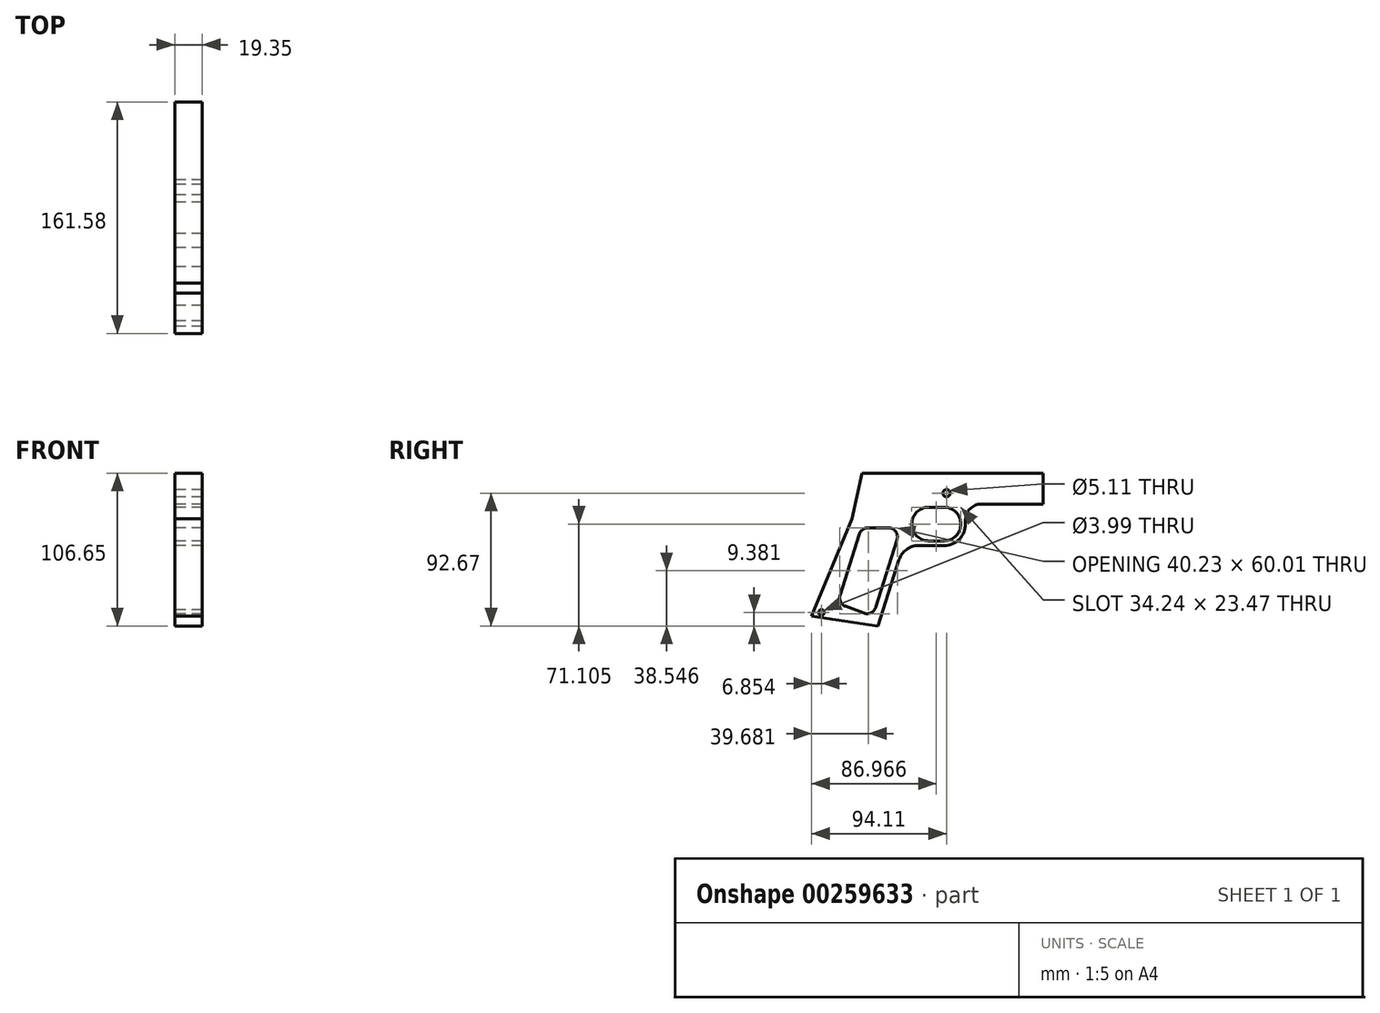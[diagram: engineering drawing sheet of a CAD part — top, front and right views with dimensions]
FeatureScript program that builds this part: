
annotation { "Feature Type Name" : "Feature", "Feature Type Description" : "" }
export const myFeature = defineFeature(function(context is Context, id is Id, definition is map)
    precondition{}
    {
        {
            var Q0;
            Q0=qCreatedBy(makeId("Right.planeOp"),FACE);
            var sketch = newSketch(context, id + "F0", { "sketchPlane" : qUnion([Q0])});
            skCircle(sketch, "E0", {"center": v(0, 0) * mm, "radius": 2.55 * mm});
            skLineSegment(sketch, "E1", {"start": v(-54.8, -24.12) * mm, "end": v(-40.65, -24.12) * mm});
            skLineSegment(sketch, "E2", {"start": v(-60.85, -28.56) * mm, "end": v(-74.27, -71.12) * mm});
            skLineSegment(sketch, "E3", {"start": v(-49.51, -79.7) * mm, "end": v(-34.6, -32.38) * mm});
            skLineSegment(sketch, "E4", {"start": v(-70.45, -78.97) * mm, "end": v(-57.8, -83.73) * mm});
            skPoint(sketch, "E5.visualSharp", {"position": v(-59.45, -24.12) * mm});
            skArc(sketch, "E5.filletArc", {"start": v(-54.8, -24.12) * mm, "mid": v(-58.55, -25.35) * mm, "end": v(-60.85, -28.56) * mm});
            skPoint(sketch, "E6.visualSharp", {"position": v(-31.99, -24.12) * mm});
            skArc(sketch, "E6.filletArc", {"start": v(-34.6, -32.38) * mm, "mid": v(-35.53, -26.71) * mm, "end": v(-40.65, -24.12) * mm});
            skPoint(sketch, "E7.visualSharp", {"position": v(-51.53, -86.1) * mm});
            skArc(sketch, "E7.filletArc", {"start": v(-57.8, -83.73) * mm, "mid": v(-52.79, -83.5) * mm, "end": v(-49.51, -79.7) * mm});
            skPoint(sketch, "E8.visualSharp", {"position": v(-76.08, -76.85) * mm});
            skArc(sketch, "E8.filletArc", {"start": v(-74.27, -71.12) * mm, "mid": v(-73.92, -75.8) * mm, "end": v(-70.45, -78.97) * mm});
            skLineSegment(sketch, "E9", {"start": v(-47.72, -92.67) * mm, "end": v(-33.17, -46.54) * mm});
            skArc(sketch, "E10", {"start": v(-12.53, -9.83) * mm, "mid": v(-24.26, -21.56) * mm, "end": v(-12.53, -33.3) * mm});
            skArc(sketch, "E11", {"start": v(-1.76, -33.3) * mm, "mid": v(9.98, -21.56) * mm, "end": v(-1.76, -9.83) * mm});
            skLineSegment(sketch, "E12", {"start": v(-12.53, -9.83) * mm, "end": v(-1.76, -9.83) * mm});
            skLineSegment(sketch, "E13", {"start": v(-12.53, -33.3) * mm, "end": v(-1.76, -33.3) * mm});
            skArc(sketch, "E14", {"start": v(-1.76, -36.55) * mm, "mid": v(8.84, -32.16) * mm, "end": v(13.23, -21.56) * mm});
            skLineSegment(sketch, "E15", {"start": v(-1.76, -36.55) * mm, "end": v(-19.54, -36.55) * mm});
            skArc(sketch, "E16.filletArc", {"start": v(-19.54, -36.55) * mm, "mid": v(-28, -39.32) * mm, "end": v(-33.17, -46.54) * mm});
            skLineSegment(sketch, "E17", {"start": v(67.47, -7.62) * mm, "end": v(24.34, -7.62) * mm});
            skLineSegment(sketch, "E18", {"start": v(13.23, -21.56) * mm, "end": v(13.23, -18.73) * mm});
            skPoint(sketch, "E18.startSnap0", {"position": v(9.98, -21.56) * mm});
            skArc(sketch, "E19.filletArc", {"start": v(24.34, -7.62) * mm, "mid": v(16.48, -10.87) * mm, "end": v(13.23, -18.73) * mm});
            skLineSegment(sketch, "E20", {"start": v(67.47, 13.98) * mm, "end": v(-58.84, 13.98) * mm});
            skLineSegment(sketch, "E21", {"start": v(67.47, 13.98) * mm, "end": v(67.47, -7.62) * mm});
            skCircle(sketch, "E22", {"center": v(-87.26, -83.29) * mm, "radius": 2 * mm});
            skLineSegment(sketch, "E23", {"start": v(-47.72, -92.67) * mm, "end": v(-94.1, -85.82) * mm});
            skLineSegment(sketch, "E24", {"start": v(-94.1, -85.82) * mm, "end": v(-65.93, -17.8) * mm});
            skLineSegment(sketch, "E25", {"start": v(-58.84, 13.98) * mm, "end": v(-65.93, -17.8) * mm});
            skSolve(sketch);
        }
        {
            var Q0;
            Q0 = qSketchRegion(id + "F0", true);
            extrude(context, id + "F1", {"entities" : qUnion([Q0]), "depth" : 19.35 * mm});
        }
    });
